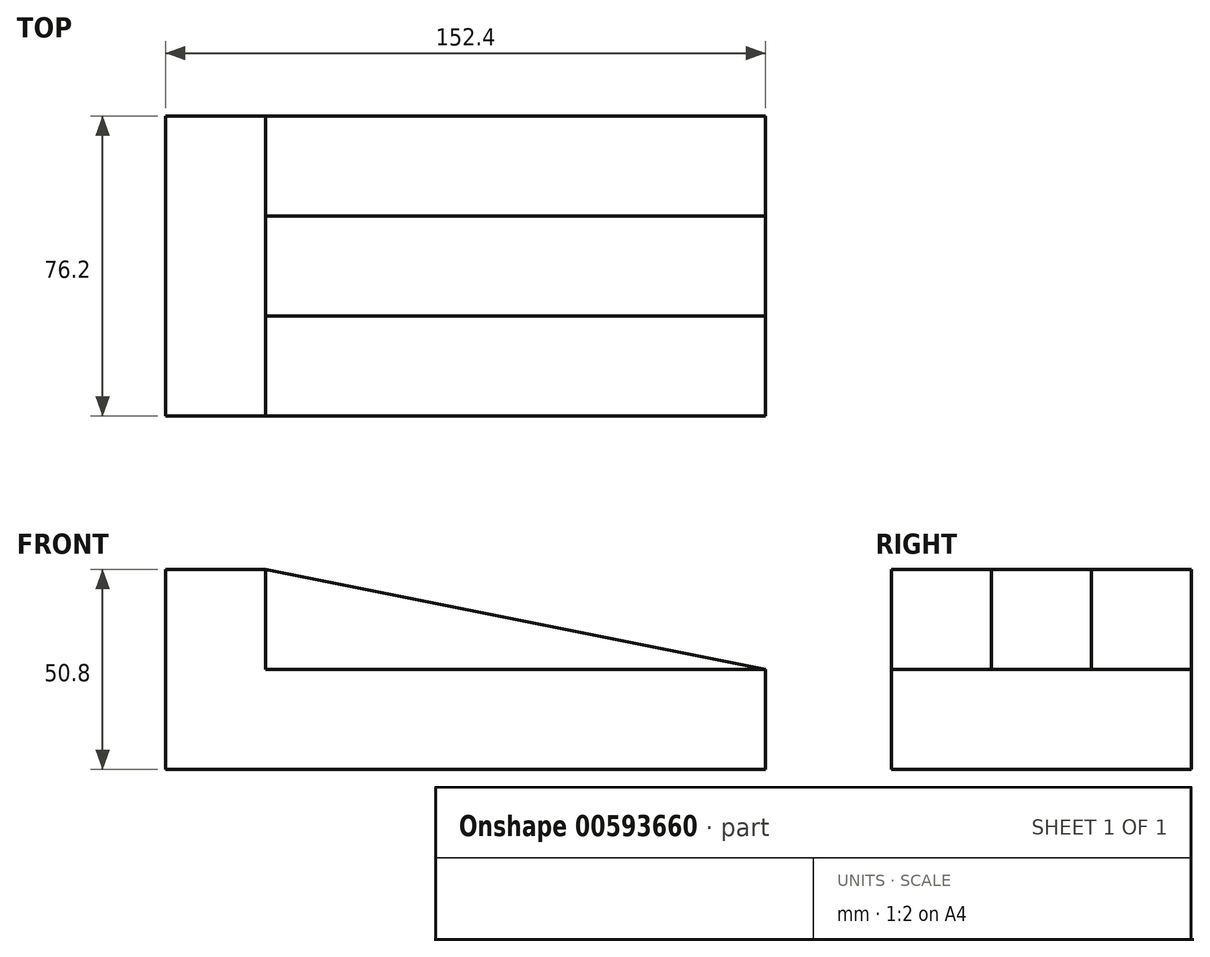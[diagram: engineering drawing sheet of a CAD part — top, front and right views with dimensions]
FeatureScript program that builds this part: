
annotation { "Feature Type Name" : "Feature", "Feature Type Description" : "" }
export const myFeature = defineFeature(function(context is Context, id is Id, definition is map)
    precondition{}
    {
        {
            var Q0;
            Q0=qCreatedBy(makeId("Front.planeOp"),FACE);
            var sketch = newSketch(context, id + "F0", { "sketchPlane" : qUnion([Q0])});
            skLineSegment(sketch, "E0", {"start": v(152.4, 0) * mm, "end": v(0, 0) * mm});
            skLineSegment(sketch, "E1", {"start": v(0, 0) * mm, "end": v(0, 50.8) * mm});
            skLineSegment(sketch, "E2", {"start": v(0, 50.8) * mm, "end": v(152.4, 50.8) * mm});
            skLineSegment(sketch, "E3", {"start": v(152.4, 50.8) * mm, "end": v(152.4, 0) * mm});
            skSolve(sketch);
        }
        {
            var Q0;
            Q0 = qSketchRegion(id + "F0", true);
            extrude(context, id + "F1", {"entities" : qUnion([Q0]), "oppositeDirection" : true, "depth" : 76.2 * mm, "offsetDistance" : 25.4 * mm});
        }
        {
            var Q0;
            Q0=makeQuery(id+"F1.opExtrude","CAP_FACE",FACE,{"disambiguationData":[OSD([sQuery(id+"F0.wireOp",EDGE,"E0"),sQuery(id+"F0.wireOp",EDGE,"E1"),sQuery(id+"F0.wireOp",EDGE,"E2"),sQuery(id+"F0.wireOp",EDGE,"E3")])],"isStart":true});
            var sketch = newSketch(context, id + "F2", { "sketchPlane" : qUnion([Q0])});
            skLineSegment(sketch, "E4", {"start": v(0, 50.8) * mm, "end": v(25.4, 50.8) * mm});
            skLineSegment(sketch, "E5", {"start": v(25.4, 50.8) * mm, "end": v(25.4, 25.4) * mm});
            skLineSegment(sketch, "E6", {"start": v(25.4, 25.4) * mm, "end": v(152.4, 25.4) * mm});
            skLineSegment(sketch, "E7", {"start": v(152.4, 25.4) * mm, "end": v(25.4, 50.8) * mm});
            skSolve(sketch);
        }
        {
            var Q0;
            {var subQ0=sQuery(id+"F2.wireOp",EDGE,"E7");Q0=makeQuery(id+"F2.imprint","IMPRINT",FACE,{"disambiguationData":[TD([[makeQuery(id+"F2.imprint","IMPRINT",EDGE,{"derivedFrom":subQ0}),-1.0]])]});}
            extrude(context, id + "F3", {"entities" : qUnion([Q0]), "operationType" : NewBodyOperationType.REMOVE, "oppositeDirection" : true, "depth" : 76.2 * mm, "offsetDistance" : 25.4 * mm});
        }
        {
            var Q0;
            Q0 = qSketchRegion(id + "F2", true);
            extrude(context, id + "F4", {"entities" : qUnion([Q0]), "operationType" : NewBodyOperationType.REMOVE, "oppositeDirection" : true, "depth" : 25.4 * mm, "offsetDistance" : 25.4 * mm});
        }
        {
            var Q0;
            Q0=makeQuery(id+"F1.opExtrude","CAP_FACE",FACE,{"disambiguationData":[OSD([sQuery(id+"F0.wireOp",EDGE,"E0"),sQuery(id+"F0.wireOp",EDGE,"E1"),sQuery(id+"F0.wireOp",EDGE,"E2"),sQuery(id+"F0.wireOp",EDGE,"E3")])],"isStart":false});
            var sketch = newSketch(context, id + "F5", { "sketchPlane" : qUnion([Q0])});
            skLineSegment(sketch, "E8", {"start": v(-25.4, 50.8) * mm, "end": v(-25.4, 25.4) * mm});
            skLineSegment(sketch, "E9", {"start": v(-25.4, 25.4) * mm, "end": v(-152.4, 25.4) * mm});
            skSolve(sketch);
        }
        {
            var Q0;
            Q0=makeQuery(id+"F5.imprint","IMPRINT",FACE,{"disambiguationData":[TD([[makeQuery(id+"F5.imprint","IMPRINT",EDGE,{"derivedFrom":sQuery(id+"F5.wireOp",EDGE,"E8")}),-1.0]])]});
            extrude(context, id + "F6", {"entities" : qUnion([Q0]), "operationType" : NewBodyOperationType.REMOVE, "oppositeDirection" : true, "depth" : 25.4 * mm, "offsetDistance" : 25.4 * mm});
        }
    });
